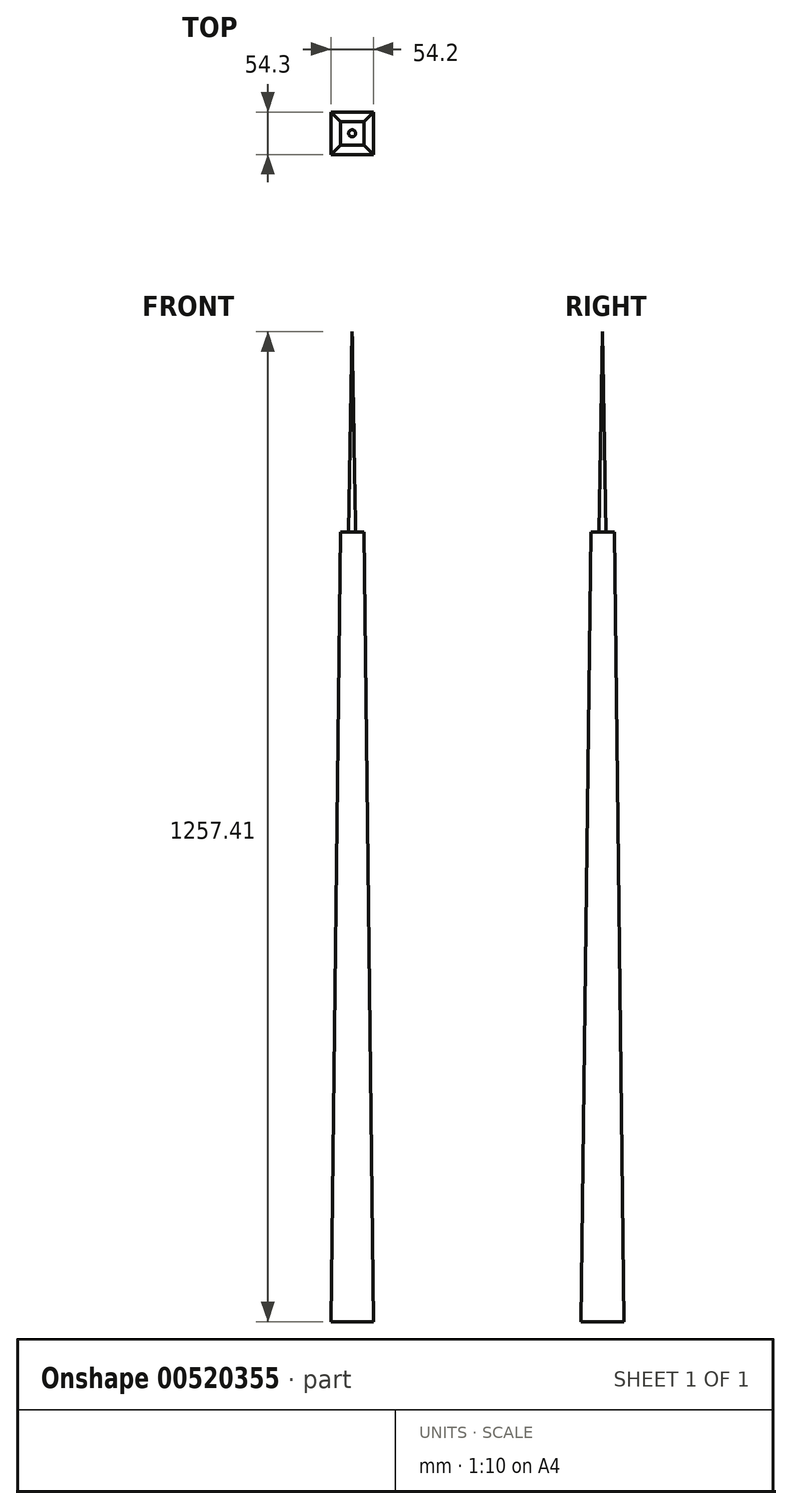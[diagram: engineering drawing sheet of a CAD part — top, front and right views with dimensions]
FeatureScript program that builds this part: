
annotation { "Feature Type Name" : "Feature", "Feature Type Description" : "" }
export const myFeature = defineFeature(function(context is Context, id is Id, definition is map)
    precondition{}
    {
        {
            var Q0;
            Q0=qCreatedBy(makeId("Top.planeOp"),FACE);
            var sketch = newSketch(context, id + "F0", { "sketchPlane" : qUnion([Q0])});
            skLineSegment(sketch, "E0.bottom", {"start": v(27.1, -27.15) * mm, "end": v(-27.1, -27.15) * mm});
            skLineSegment(sketch, "E0.top", {"start": v(27.1, 27.15) * mm, "end": v(-27.1, 27.15) * mm});
            skLineSegment(sketch, "E0.left", {"start": v(27.1, -27.15) * mm, "end": v(27.1, 27.15) * mm});
            skLineSegment(sketch, "E0.right", {"start": v(-27.1, -27.15) * mm, "end": v(-27.1, 27.15) * mm});
            skPoint(sketch, "E0.middle", {"position": v(0, 0) * mm});
            skSolve(sketch);
        }
        {
            var Q0;
            Q0=makeQuery(id+"F0.imprint","IMPRINT",FACE,{"disambiguationData":[TD([[makeQuery(id+"F0.imprint","IMPRINT",EDGE,{"derivedFrom":sQuery(id+"F0.wireOp",EDGE,"J9EcX12F-zg4u-qeEq-1IbT-foyMk7RzKAtM.bottom")}),-1.0]])]});
            var Q1;
            Q1=makeQuery(id+"F0.imprint","IMPRINT",FACE,{"disambiguationData":[TD([[makeQuery(id+"F0.imprint","IMPRINT",EDGE,{"derivedFrom":sQuery(id+"F0.wireOp",EDGE,"E0.bottom")}),-1.0]])]});
            extrude(context, id + "F1", {"entities" : qUnion([Q0, Q1]), "depth" : 1003.3 * mm, "offsetDistance" : 25.4 * mm, "hasDraft" : true, "draftAngle" : 0.7 * degree, "draftPullDirection" : true});
        }
        {
            var Q0;
            Q0=makeQuery(id+"F1.opExtrude","CAP_FACE",FACE,{"disambiguationData":[OSD([sQuery(id+"F0.wireOp",EDGE,"E0.bottom"),sQuery(id+"F0.wireOp",EDGE,"E0.top"),sQuery(id+"F0.wireOp",EDGE,"E0.left"),sQuery(id+"F0.wireOp",EDGE,"E0.right")])],"isStart":false});
            var sketch = newSketch(context, id + "F2", { "sketchPlane" : qUnion([Q0])});
            skCircle(sketch, "E1", {"center": v(0, 0) * mm, "radius": 4.44 * mm});
            skSolve(sketch);
        }
        {
            var Q0;
            Q0=makeQuery(id+"F2.imprint","IMPRINT",FACE,{"disambiguationData":[TD([[makeQuery(id+"F2.imprint","IMPRINT",EDGE,{"derivedFrom":sQuery(id+"F2.wireOp",EDGE,"E1")}),1.0]])]});
            extrude(context, id + "F3", {"entities" : qUnion([Q0]), "operationType" : NewBodyOperationType.ADD, "depth" : 630.43 * mm, "offsetDistance" : 25.4 * mm, "hasDraft" : true, "draftAngle" : 1 * degree, "draftPullDirection" : true});
        }
    });
